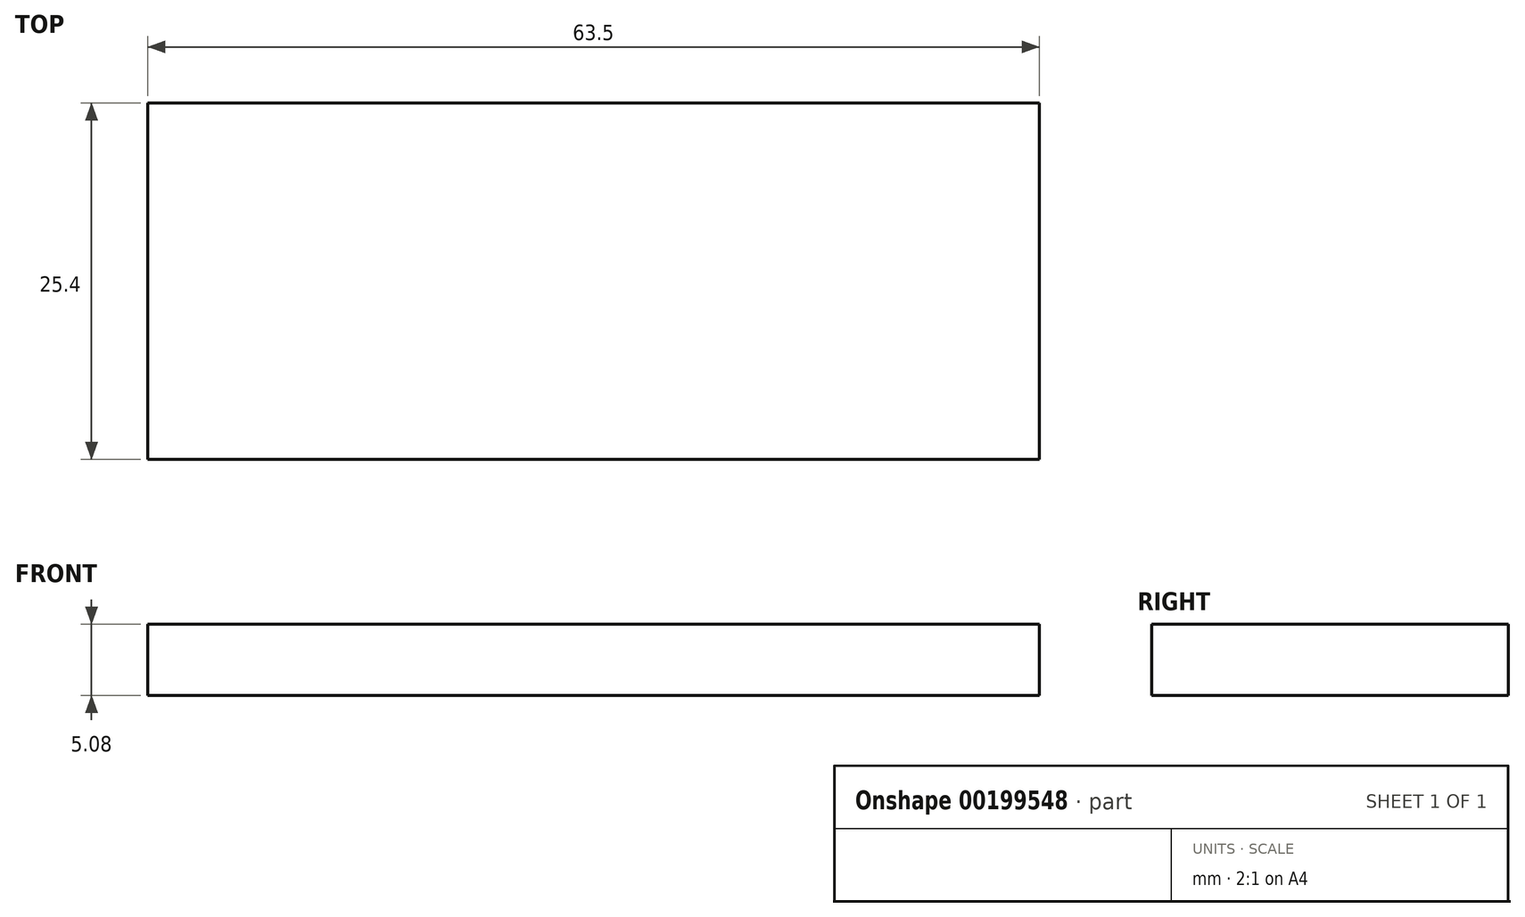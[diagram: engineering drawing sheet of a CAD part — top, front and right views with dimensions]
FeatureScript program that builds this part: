
annotation { "Feature Type Name" : "Feature", "Feature Type Description" : "" }
export const myFeature = defineFeature(function(context is Context, id is Id, definition is map)
    precondition{}
    {
        {
            var Q0;
            Q0=qCreatedBy(makeId("Top.planeOp"),FACE);
            var sketch = newSketch(context, id + "F0", { "sketchPlane" : qUnion([Q0])});
            skLineSegment(sketch, "E0.bottom", {"start": v(31.75, -12.7) * mm, "end": v(-31.75, -12.7) * mm});
            skLineSegment(sketch, "E0.top", {"start": v(31.75, 12.7) * mm, "end": v(-31.75, 12.7) * mm});
            skLineSegment(sketch, "E0.left", {"start": v(31.75, -12.7) * mm, "end": v(31.75, 12.7) * mm});
            skLineSegment(sketch, "E0.right", {"start": v(-31.75, -12.7) * mm, "end": v(-31.75, 12.7) * mm});
            skPoint(sketch, "E0.middle", {"position": v(0, 0) * mm});
            skSolve(sketch);
        }
        {
            var Q0;
            Q0=makeQuery(id+"F0.imprint","IMPRINT",FACE,{"disambiguationData":[TD([[makeQuery(id+"F0.imprint","IMPRINT",EDGE,{"derivedFrom":sQuery(id+"F0.wireOp",EDGE,"E0.bottom")}),-1.0]])]});
            extrude(context, id + "F1", {"entities" : qUnion([Q0]), "depth" : 5.08 * mm});
        }
    });
